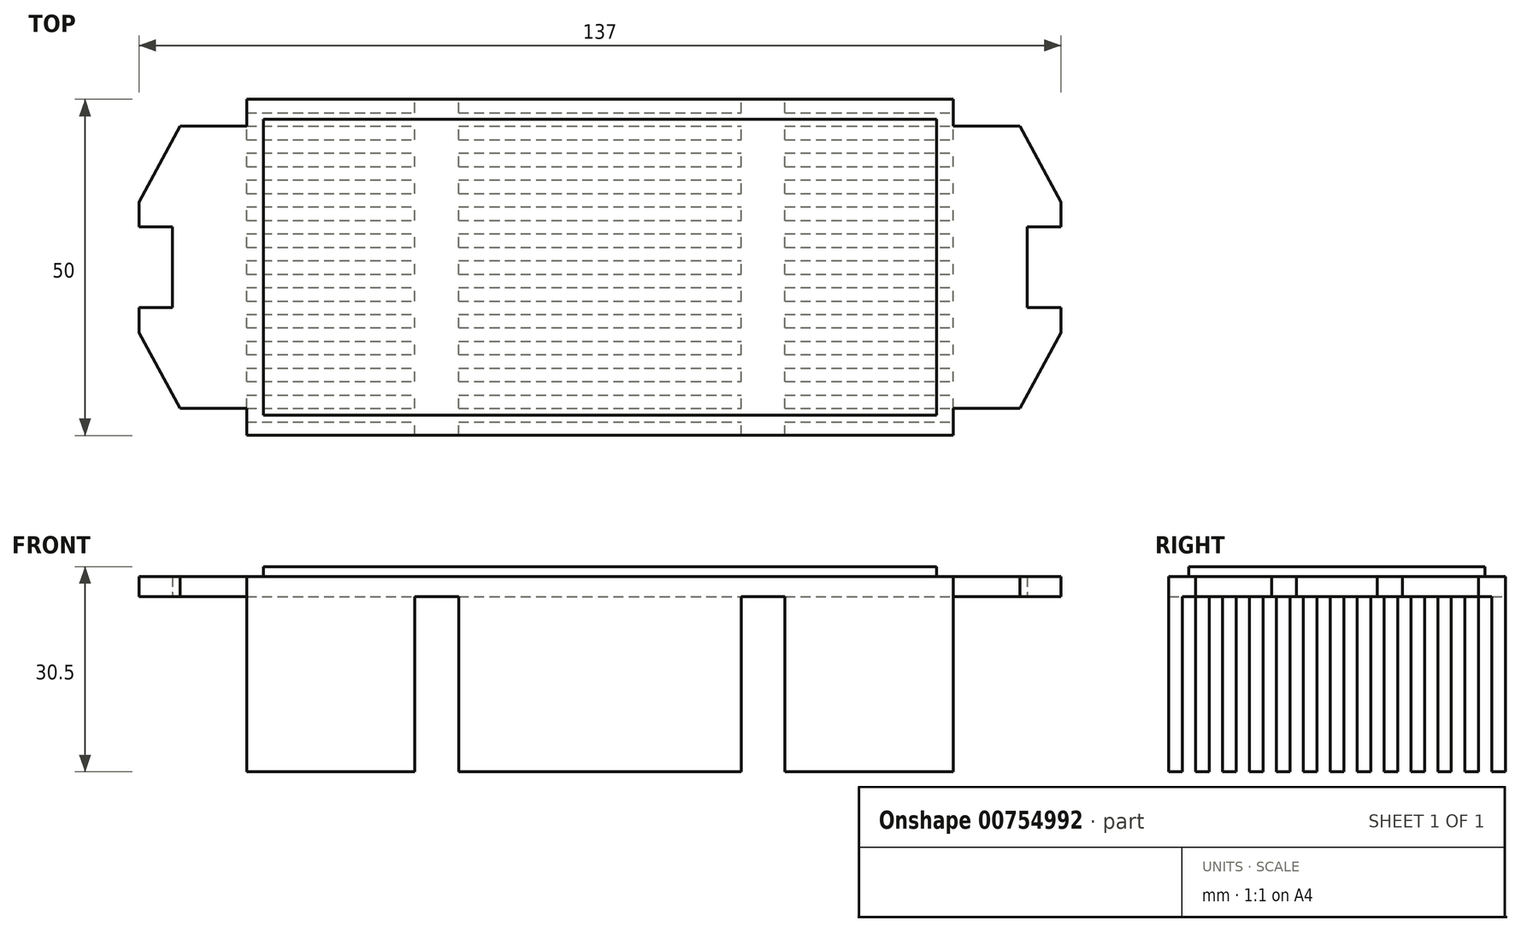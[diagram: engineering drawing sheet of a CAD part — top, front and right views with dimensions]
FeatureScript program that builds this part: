
annotation { "Feature Type Name" : "Feature", "Feature Type Description" : "" }
export const myFeature = defineFeature(function(context is Context, id is Id, definition is map)
    precondition{}
    {
        {
            var Q0;
            Q0=qCreatedBy(makeId("Top.planeOp"),FACE);
            var sketch = newSketch(context, id + "F0", { "sketchPlane" : qUnion([Q0])});
            skLineSegment(sketch, "E0.bottom", {"start": v(-43.4, 26.63) * mm, "end": v(61.6, 26.63) * mm});
            skLineSegment(sketch, "E0.top", {"start": v(-43.4, -23.37) * mm, "end": v(61.6, -23.37) * mm});
            skLineSegment(sketch, "E0.left", {"start": v(-59.4, 11.35) * mm, "end": v(-59.4, 7.63) * mm});
            skLineSegment(sketch, "E0.right", {"start": v(77.6, 11.35) * mm, "end": v(77.6, 7.63) * mm});
            skLineSegment(sketch, "E1.bottom", {"start": v(-59.4, 7.63) * mm, "end": v(-54.4, 7.63) * mm});
            skLineSegment(sketch, "E1.top", {"start": v(-59.4, -4.37) * mm, "end": v(-54.4, -4.37) * mm});
            skLineSegment(sketch, "E1.right", {"start": v(-54.4, 7.63) * mm, "end": v(-54.4, -4.37) * mm});
            skLineSegment(sketch, "E2.bottom", {"start": v(77.6, 7.63) * mm, "end": v(72.6, 7.63) * mm});
            skLineSegment(sketch, "E2.top", {"start": v(77.6, -4.37) * mm, "end": v(72.6, -4.37) * mm});
            skLineSegment(sketch, "E2.right", {"start": v(72.6, 7.63) * mm, "end": v(72.6, -4.37) * mm});
            skLineSegment(sketch, "E3.bottom", {"start": v(-75.96, 42.25) * mm, "end": v(-43.4, 42.25) * mm});
            skLineSegment(sketch, "E3.top", {"start": v(-53.27, 22.63) * mm, "end": v(-43.4, 22.63) * mm});
            skLineSegment(sketch, "E3.left", {"start": v(-75.96, 42.25) * mm, "end": v(-75.96, 22.63) * mm});
            skLineSegment(sketch, "E3.right", {"start": v(-43.4, 26.63) * mm, "end": v(-43.4, 22.63) * mm});
            skLineSegment(sketch, "E4.bottom", {"start": v(91.92, 37.83) * mm, "end": v(61.6, 37.83) * mm});
            skLineSegment(sketch, "E4.top", {"start": v(71.47, 22.63) * mm, "end": v(61.6, 22.63) * mm});
            skLineSegment(sketch, "E4.left", {"start": v(91.92, 37.83) * mm, "end": v(91.92, 22.63) * mm});
            skLineSegment(sketch, "E4.right", {"start": v(61.6, 26.63) * mm, "end": v(61.6, 22.63) * mm});
            skLineSegment(sketch, "E5.bottom", {"start": v(82.37, -42.83) * mm, "end": v(61.6, -42.83) * mm});
            skLineSegment(sketch, "E5.top", {"start": v(71.47, -19.37) * mm, "end": v(61.6, -19.37) * mm});
            skLineSegment(sketch, "E5.left", {"start": v(82.37, -42.83) * mm, "end": v(82.37, -19.37) * mm});
            skLineSegment(sketch, "E5.right", {"start": v(61.6, -23.37) * mm, "end": v(61.6, -19.37) * mm});
            skLineSegment(sketch, "E6.bottom", {"start": v(-65.96, -42.44) * mm, "end": v(-43.4, -42.44) * mm});
            skLineSegment(sketch, "E6.top", {"start": v(-53.27, -19.37) * mm, "end": v(-43.4, -19.37) * mm});
            skLineSegment(sketch, "E6.left", {"start": v(-65.96, -42.44) * mm, "end": v(-65.96, -19.37) * mm});
            skLineSegment(sketch, "E6.right", {"start": v(-43.4, -23.37) * mm, "end": v(-43.4, -19.37) * mm});
            skLineSegment(sketch, "E7.trimOffspring", {"start": v(-59.4, -4.37) * mm, "end": v(-59.4, -8.08) * mm});
            skLineSegment(sketch, "E8.trimOffspring", {"start": v(77.6, -4.37) * mm, "end": v(77.6, -8.08) * mm});
            skLineSegment(sketch, "E9", {"start": v(-59.4, 11.35) * mm, "end": v(-53.27, 22.63) * mm});
            skLineSegment(sketch, "E10", {"start": v(-54.4, 1.63) * mm, "end": v(-23.27, 1.63) * mm});
            skLineSegment(sketch, "E11", {"start": v(9.1, 26.63) * mm, "end": v(9.1, 11.73) * mm});
            skLineSegment(sketch, "E12.MirrorCS", {"start": v(77.6, 11.35) * mm, "end": v(71.47, 22.63) * mm});
            skLineSegment(sketch, "E13.MirrorCS", {"start": v(-59.4, -8.08) * mm, "end": v(-53.27, -19.37) * mm});
            skLineSegment(sketch, "E14.MirrorCS", {"start": v(77.6, -8.08) * mm, "end": v(71.47, -19.37) * mm});
            skSolve(sketch);
        }
        {
            var Q0;
            Q0=makeQuery(id+"F0.imprint","IMPRINT",FACE,{"disambiguationData":[TD([[makeQuery(id+"F0.imprint","IMPRINT",EDGE,{"derivedFrom":sQuery(id+"F0.wireOp",EDGE,"E0.top")}),1.0]])]});
            extrude(context, id + "F1", {"entities" : qUnion([Q0]), "depth" : 3 * mm, "offsetDistance" : 25 * mm});
        }
        {
            var Q0;
            Q0=makeQuery(id+"F1.opExtrude","CAP_FACE",FACE,{"disambiguationData":[OSD([sQuery(id+"F0.wireOp",EDGE,"E0.bottom"),sQuery(id+"F0.wireOp",EDGE,"E0.top"),sQuery(id+"F0.wireOp",EDGE,"E0.left"),sQuery(id+"F0.wireOp",EDGE,"E0.right"),sQuery(id+"F0.wireOp",EDGE,"E1.bottom"),sQuery(id+"F0.wireOp",EDGE,"E1.top"),sQuery(id+"F0.wireOp",EDGE,"E1.right"),sQuery(id+"F0.wireOp",EDGE,"E2.bottom"),sQuery(id+"F0.wireOp",EDGE,"E2.top"),sQuery(id+"F0.wireOp",EDGE,"E2.right"),sQuery(id+"F0.wireOp",EDGE,"E3.top"),sQuery(id+"F0.wireOp",EDGE,"E3.right"),sQuery(id+"F0.wireOp",EDGE,"E4.top"),sQuery(id+"F0.wireOp",EDGE,"E4.right"),sQuery(id+"F0.wireOp",EDGE,"E5.top"),sQuery(id+"F0.wireOp",EDGE,"E5.right"),sQuery(id+"F0.wireOp",EDGE,"E6.top"),sQuery(id+"F0.wireOp",EDGE,"E6.right"),sQuery(id+"F0.wireOp",EDGE,"E7.trimOffspring"),sQuery(id+"F0.wireOp",EDGE,"E8.trimOffspring"),sQuery(id+"F0.wireOp",EDGE,"E9"),sQuery(id+"F0.wireOp",EDGE,"E12.MirrorCS"),sQuery(id+"F0.wireOp",EDGE,"E13.MirrorCS"),sQuery(id+"F0.wireOp",EDGE,"E14.MirrorCS")])],"isStart":false});
            var sketch = newSketch(context, id + "F2", { "sketchPlane" : qUnion([Q0])});
            skLineSegment(sketch, "E15.bottom", {"start": v(-40.9, 23.63) * mm, "end": v(59.1, 23.63) * mm});
            skLineSegment(sketch, "E15.top", {"start": v(-40.9, -20.37) * mm, "end": v(59.1, -20.37) * mm});
            skLineSegment(sketch, "E15.left", {"start": v(-40.9, 23.63) * mm, "end": v(-40.9, -20.37) * mm});
            skLineSegment(sketch, "E15.right", {"start": v(59.1, 23.63) * mm, "end": v(59.1, -20.37) * mm});
            skSolve(sketch);
        }
        {
            var Q0;
            Q0 = qSketchRegion(id + "F2", true);
            extrude(context, id + "F3", {"entities" : qUnion([Q0]), "operationType" : NewBodyOperationType.ADD, "depth" : 1.5 * mm, "offsetDistance" : 25 * mm});
        }
        {
            var Q0;
            Q0=makeQuery(id+"F1.opExtrude","CAP_FACE",FACE,{"disambiguationData":[OSD([sQuery(id+"F0.wireOp",EDGE,"E0.bottom"),sQuery(id+"F0.wireOp",EDGE,"E0.top"),sQuery(id+"F0.wireOp",EDGE,"E0.left"),sQuery(id+"F0.wireOp",EDGE,"E0.right"),sQuery(id+"F0.wireOp",EDGE,"E1.bottom"),sQuery(id+"F0.wireOp",EDGE,"E1.top"),sQuery(id+"F0.wireOp",EDGE,"E1.right"),sQuery(id+"F0.wireOp",EDGE,"E2.bottom"),sQuery(id+"F0.wireOp",EDGE,"E2.top"),sQuery(id+"F0.wireOp",EDGE,"E2.right"),sQuery(id+"F0.wireOp",EDGE,"E3.top"),sQuery(id+"F0.wireOp",EDGE,"E3.right"),sQuery(id+"F0.wireOp",EDGE,"E4.top"),sQuery(id+"F0.wireOp",EDGE,"E4.right"),sQuery(id+"F0.wireOp",EDGE,"E5.top"),sQuery(id+"F0.wireOp",EDGE,"E5.right"),sQuery(id+"F0.wireOp",EDGE,"E6.top"),sQuery(id+"F0.wireOp",EDGE,"E6.right"),sQuery(id+"F0.wireOp",EDGE,"E7.trimOffspring"),sQuery(id+"F0.wireOp",EDGE,"E8.trimOffspring"),sQuery(id+"F0.wireOp",EDGE,"E9"),sQuery(id+"F0.wireOp",EDGE,"E12.MirrorCS"),sQuery(id+"F0.wireOp",EDGE,"E13.MirrorCS"),sQuery(id+"F0.wireOp",EDGE,"E14.MirrorCS")])],"isStart":true});
            var sketch = newSketch(context, id + "F4", { "sketchPlane" : qUnion([Q0])});
            skLineSegment(sketch, "E16.bottom", {"start": v(-43.4, 23.37) * mm, "end": v(61.6, 23.37) * mm});
            skLineSegment(sketch, "E16.top", {"start": v(-43.4, 21.37) * mm, "end": v(61.6, 21.37) * mm});
            skLineSegment(sketch, "E16.left", {"start": v(-43.4, 23.37) * mm, "end": v(-43.4, 21.37) * mm});
            skLineSegment(sketch, "E16.right", {"start": v(61.6, 23.37) * mm, "end": v(61.6, 21.37) * mm});
            skLineSegment(sketch, "E17.0.1.0", {"start": v(-43.4, 19.37) * mm, "end": v(61.6, 19.37) * mm});
            skLineSegment(sketch, "E17.0.1.1", {"start": v(-43.4, 17.37) * mm, "end": v(61.6, 17.37) * mm});
            skLineSegment(sketch, "E17.0.1.2", {"start": v(61.6, 19.37) * mm, "end": v(61.6, 17.37) * mm});
            skLineSegment(sketch, "E17.0.1.3", {"start": v(-43.4, 19.37) * mm, "end": v(-43.4, 17.37) * mm});
            skLineSegment(sketch, "E17.0.2.0", {"start": v(-43.4, 15.37) * mm, "end": v(61.6, 15.37) * mm});
            skLineSegment(sketch, "E17.0.2.1", {"start": v(-43.4, 13.37) * mm, "end": v(61.6, 13.37) * mm});
            skLineSegment(sketch, "E17.0.2.2", {"start": v(61.6, 15.37) * mm, "end": v(61.6, 13.37) * mm});
            skLineSegment(sketch, "E17.0.2.3", {"start": v(-43.4, 15.37) * mm, "end": v(-43.4, 13.37) * mm});
            skLineSegment(sketch, "E17.0.3.0", {"start": v(-43.4, 11.37) * mm, "end": v(61.6, 11.37) * mm});
            skLineSegment(sketch, "E17.0.3.1", {"start": v(-43.4, 9.37) * mm, "end": v(61.6, 9.37) * mm});
            skLineSegment(sketch, "E17.0.3.2", {"start": v(61.6, 11.37) * mm, "end": v(61.6, 9.37) * mm});
            skLineSegment(sketch, "E17.0.3.3", {"start": v(-43.4, 11.37) * mm, "end": v(-43.4, 9.37) * mm});
            skLineSegment(sketch, "E17.0.4.0", {"start": v(-43.4, 7.37) * mm, "end": v(61.6, 7.37) * mm});
            skLineSegment(sketch, "E17.0.4.1", {"start": v(-43.4, 5.37) * mm, "end": v(61.6, 5.37) * mm});
            skLineSegment(sketch, "E17.0.4.2", {"start": v(61.6, 7.37) * mm, "end": v(61.6, 5.37) * mm});
            skLineSegment(sketch, "E17.0.4.3", {"start": v(-43.4, 7.37) * mm, "end": v(-43.4, 5.37) * mm});
            skLineSegment(sketch, "E17.0.5.0", {"start": v(-43.4, 3.37) * mm, "end": v(61.6, 3.37) * mm});
            skLineSegment(sketch, "E17.0.5.1", {"start": v(-43.4, 1.37) * mm, "end": v(61.6, 1.37) * mm});
            skLineSegment(sketch, "E17.0.5.2", {"start": v(61.6, 3.37) * mm, "end": v(61.6, 1.37) * mm});
            skLineSegment(sketch, "E17.0.5.3", {"start": v(-43.4, 3.37) * mm, "end": v(-43.4, 1.37) * mm});
            skLineSegment(sketch, "E17.0.6.0", {"start": v(-43.4, -0.63) * mm, "end": v(61.6, -0.63) * mm});
            skLineSegment(sketch, "E17.0.6.1", {"start": v(-43.4, -2.63) * mm, "end": v(61.6, -2.63) * mm});
            skLineSegment(sketch, "E17.0.6.2", {"start": v(61.6, -0.63) * mm, "end": v(61.6, -2.63) * mm});
            skLineSegment(sketch, "E17.0.6.3", {"start": v(-43.4, -0.63) * mm, "end": v(-43.4, -2.63) * mm});
            skLineSegment(sketch, "E17.0.7.0", {"start": v(-43.4, -4.63) * mm, "end": v(61.6, -4.63) * mm});
            skLineSegment(sketch, "E17.0.7.1", {"start": v(-43.4, -6.63) * mm, "end": v(61.6, -6.63) * mm});
            skLineSegment(sketch, "E17.0.7.2", {"start": v(61.6, -4.63) * mm, "end": v(61.6, -6.63) * mm});
            skLineSegment(sketch, "E17.0.7.3", {"start": v(-43.4, -4.63) * mm, "end": v(-43.4, -6.63) * mm});
            skLineSegment(sketch, "E17.0.8.0", {"start": v(-43.4, -8.63) * mm, "end": v(61.6, -8.63) * mm});
            skLineSegment(sketch, "E17.0.8.1", {"start": v(-43.4, -10.63) * mm, "end": v(61.6, -10.63) * mm});
            skLineSegment(sketch, "E17.0.8.2", {"start": v(61.6, -8.63) * mm, "end": v(61.6, -10.63) * mm});
            skLineSegment(sketch, "E17.0.8.3", {"start": v(-43.4, -8.63) * mm, "end": v(-43.4, -10.63) * mm});
            skLineSegment(sketch, "E17.0.9.0", {"start": v(-43.4, -12.63) * mm, "end": v(61.6, -12.63) * mm});
            skLineSegment(sketch, "E17.0.9.1", {"start": v(-43.4, -14.63) * mm, "end": v(61.6, -14.63) * mm});
            skLineSegment(sketch, "E17.0.9.2", {"start": v(61.6, -12.63) * mm, "end": v(61.6, -14.63) * mm});
            skLineSegment(sketch, "E17.0.9.3", {"start": v(-43.4, -12.63) * mm, "end": v(-43.4, -14.63) * mm});
            skLineSegment(sketch, "E17.0.10.0", {"start": v(-43.4, -16.63) * mm, "end": v(61.6, -16.63) * mm});
            skLineSegment(sketch, "E17.0.10.1", {"start": v(-43.4, -18.63) * mm, "end": v(61.6, -18.63) * mm});
            skLineSegment(sketch, "E17.0.10.2", {"start": v(61.6, -16.63) * mm, "end": v(61.6, -18.63) * mm});
            skLineSegment(sketch, "E17.0.10.3", {"start": v(-43.4, -16.63) * mm, "end": v(-43.4, -18.63) * mm});
            skLineSegment(sketch, "E17.0.11.0", {"start": v(-43.4, -20.63) * mm, "end": v(61.6, -20.63) * mm});
            skLineSegment(sketch, "E17.0.11.1", {"start": v(-43.4, -22.63) * mm, "end": v(61.6, -22.63) * mm});
            skLineSegment(sketch, "E17.0.11.2", {"start": v(61.6, -20.63) * mm, "end": v(61.6, -22.63) * mm});
            skLineSegment(sketch, "E17.0.11.3", {"start": v(-43.4, -20.63) * mm, "end": v(-43.4, -22.63) * mm});
            skLineSegment(sketch, "E17.direction1", {"start": v(-43.4, 21.37) * mm, "end": v(-18.4, 21.37) * mm, "construction": true});
            skLineSegment(sketch, "E17.direction2", {"start": v(-43.4, 21.37) * mm, "end": v(-43.4, 17.37) * mm, "construction": true});
            skLineSegment(sketch, "E18.0.0.12", {"start": v(-43.4, -24.63) * mm, "end": v(61.6, -24.63) * mm});
            skLineSegment(sketch, "E18.3.0.12", {"start": v(-43.4, -26.63) * mm, "end": v(61.6, -26.63) * mm});
            skLineSegment(sketch, "E18.6.0.12", {"start": v(61.6, -24.63) * mm, "end": v(61.6, -26.63) * mm});
            skLineSegment(sketch, "E18.9.0.12", {"start": v(-43.4, -24.63) * mm, "end": v(-43.4, -26.63) * mm});
            skSolve(sketch);
        }
        {
            var Q0;
            Q0 = qSketchRegion(id + "F4", true);
            extrude(context, id + "F5", {"entities" : qUnion([Q0]), "operationType" : NewBodyOperationType.ADD, "depth" : 26 * mm, "offsetDistance" : 25 * mm});
        }
        {
            var Q0;
            Q0=makeQuery(id+"F5.opExtrude","CAP_FACE",FACE,{"disambiguationData":[OSD([sQuery(id+"F4.wireOp",EDGE,"E16.bottom"),sQuery(id+"F4.wireOp",EDGE,"E16.top"),sQuery(id+"F4.wireOp",EDGE,"E16.left"),sQuery(id+"F4.wireOp",EDGE,"E16.right")])],"isStart":false});
            var sketch = newSketch(context, id + "F6", { "sketchPlane" : qUnion([Q0])});
            skLineSegment(sketch, "E19.bottom", {"start": v(-18.4, 30.03) * mm, "end": v(-11.9, 30.03) * mm});
            skLineSegment(sketch, "E19.top", {"start": v(-18.4, -41.17) * mm, "end": v(-11.9, -41.17) * mm});
            skLineSegment(sketch, "E19.left", {"start": v(-18.4, 30.03) * mm, "end": v(-18.4, -41.17) * mm});
            skLineSegment(sketch, "E19.right", {"start": v(-11.9, 30.03) * mm, "end": v(-11.9, -41.17) * mm});
            skLineSegment(sketch, "E20.bottom", {"start": v(30.1, 30.66) * mm, "end": v(36.6, 30.66) * mm});
            skLineSegment(sketch, "E20.top", {"start": v(30.1, -38.04) * mm, "end": v(36.6, -38.04) * mm});
            skLineSegment(sketch, "E20.left", {"start": v(30.1, 30.66) * mm, "end": v(30.1, -38.04) * mm});
            skLineSegment(sketch, "E20.right", {"start": v(36.6, 30.66) * mm, "end": v(36.6, -38.04) * mm});
            skSolve(sketch);
        }
        {
            var Q0;
            Q0 = qSketchRegion(id + "F6", true);
            extrude(context, id + "F7", {"entities" : qUnion([Q0]), "operationType" : NewBodyOperationType.REMOVE, "oppositeDirection" : true, "depth" : 26 * mm, "offsetDistance" : 25 * mm});
        }
    });
